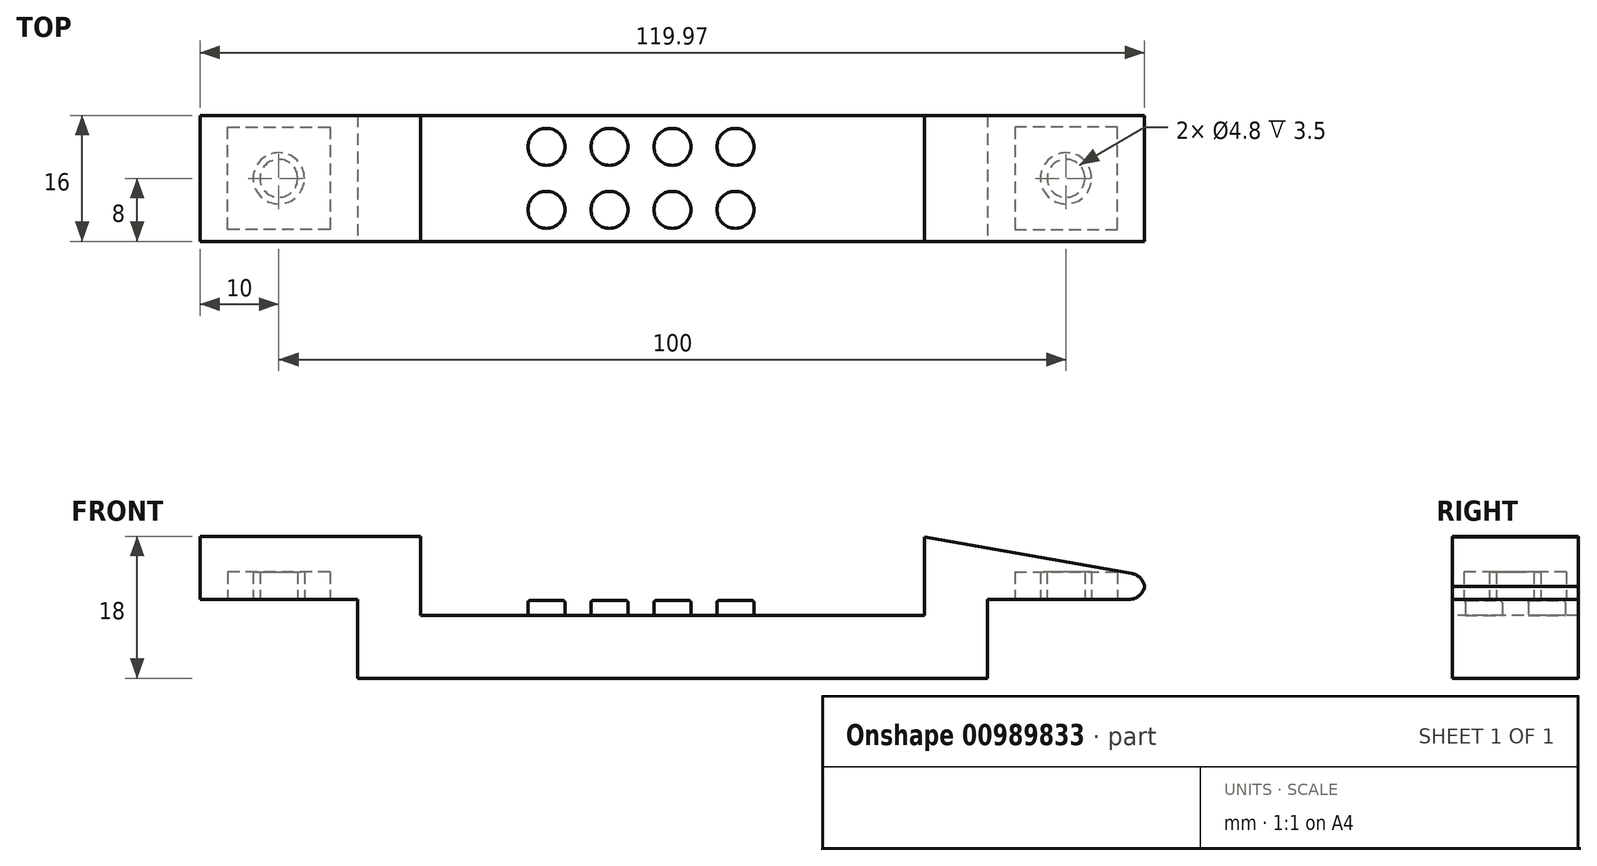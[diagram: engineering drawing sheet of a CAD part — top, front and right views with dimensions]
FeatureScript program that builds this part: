
annotation { "Feature Type Name" : "Feature", "Feature Type Description" : "" }
export const myFeature = defineFeature(function(context is Context, id is Id, definition is map)
    precondition{}
    {
        {
            var Q0;
            Q0=qCreatedBy(makeId("Front.planeOp"),FACE);
            var sketch = newSketch(context, id + "F0", { "sketchPlane" : qUnion([Q0])});
            skLineSegment(sketch, "E0", {"start": v(0, 0) * mm, "end": v(-40, 0) * mm});
            skLineSegment(sketch, "E1", {"start": v(-40, 0) * mm, "end": v(-40, 10) * mm});
            skLineSegment(sketch, "E2", {"start": v(-40, 10) * mm, "end": v(-60, 10) * mm});
            skLineSegment(sketch, "E3.0", {"start": v(-32, 18) * mm, "end": v(-60, 18) * mm});
            skLineSegment(sketch, "E3.1", {"start": v(-32, 8) * mm, "end": v(-32, 18) * mm});
            skLineSegment(sketch, "E3.2", {"start": v(0, 8) * mm, "end": v(-32, 8) * mm});
            skLineSegment(sketch, "E4", {"start": v(-60, 18) * mm, "end": v(-60, 10) * mm});
            skLineSegment(sketch, "E5", {"start": v(0, 8) * mm, "end": v(0, 0) * mm});
            skCircle(sketch, "E6", {"center": v(-50, 6) * mm, "radius": 10 * mm, "construction": true});
            skPoint(sketch, "E6.centerSnap0", {"position": v(-50, 10) * mm});
            skCircle(sketch, "E7", {"center": v(-50, 6) * mm, "radius": 12 * mm, "construction": true});
            skSolve(sketch);
        }
        {
            var Q0;
            Q0=makeQuery(id+"F0.imprint","IMPRINT",FACE,{"disambiguationData":[TD([[makeQuery(id+"F0.imprint","IMPRINT",EDGE,{"derivedFrom":sQuery(id+"F0.wireOp",EDGE,"E0")}),-1.0]])]});
            extrude(context, id + "F1", {"entities" : qUnion([Q0]), "oppositeDirection" : true, "depth" : 16 * mm, "offsetDistance" : 25 * mm});
        }
        {
            var Q0;
            Q0=makeQuery(id+"F1.opExtrude","SWEPT_FACE",FACE,{"disambiguationData":[OSD([sQuery(id+"F0.wireOp",EDGE,"E2")])]});
            var sketch = newSketch(context, id + "F2", { "sketchPlane" : qUnion([Q0])});
            skLineSegment(sketch, "E8", {"start": v(-43.5, -1.5) * mm, "end": v(-56.5, -1.5) * mm});
            skLineSegment(sketch, "E9", {"start": v(-56.5, -1.5) * mm, "end": v(-56.5, -14.5) * mm});
            skLineSegment(sketch, "E10", {"start": v(-56.5, -14.5) * mm, "end": v(-43.5, -14.5) * mm});
            skLineSegment(sketch, "E11", {"start": v(-43.5, -14.5) * mm, "end": v(-43.5, -1.5) * mm});
            skCircle(sketch, "E12.0", {"center": v(-50, -8) * mm, "radius": 2.4 * mm});
            skCircle(sketch, "E13.0", {"center": v(-50, -8) * mm, "radius": 3.25 * mm});
            skLineSegment(sketch, "E14.0", {"start": v(-42, 0) * mm, "end": v(-42, -16) * mm, "construction": true});
            skLineSegment(sketch, "E14.1", {"start": v(-42, 0) * mm, "end": v(-58, 0) * mm, "construction": true});
            skLineSegment(sketch, "E14.2", {"start": v(-58, 0) * mm, "end": v(-58, -16) * mm, "construction": true});
            skLineSegment(sketch, "E14.3", {"start": v(-42, -16) * mm, "end": v(-58, -16) * mm, "construction": true});
            skSolve(sketch);
        }
        {
            var Q0;
            Q0=makeQuery(id+"F2.imprint","IMPRINT",FACE,{"disambiguationData":[TD([[makeQuery(id+"F2.imprint","IMPRINT",EDGE,{"derivedFrom":sQuery(id+"F2.wireOp",EDGE,"E8")}),1.0]])]});
            var Q1;
            Q1=makeQuery(id+"F2.imprint","IMPRINT",FACE,{"disambiguationData":[TD([[makeQuery(id+"F2.imprint","IMPRINT",EDGE,{"derivedFrom":sQuery(id+"F2.wireOp",EDGE,"50b0818d-48c9-435e-a0db-fd159936b803.0")}),1.0]])]});
            var Q2;
            Q2=makeQuery(id+"F2.imprint","IMPRINT",FACE,{"disambiguationData":[TD([[makeQuery(id+"F2.imprint","IMPRINT",EDGE,{"derivedFrom":sQuery(id+"F2.wireOp",EDGE,"E12.0")}),1.0]])]});
            var Q3;
            Q3=makeQuery(id+"F2.imprint","IMPRINT",FACE,{"disambiguationData":[TD([[makeQuery(id+"F2.imprint","IMPRINT",EDGE,{"derivedFrom":sQuery(id+"F2.wireOp",EDGE,"9362b03a-9ce0-4955-ab87-d27d4ad72b78.0")}),1.0]])]});
            extrude(context, id + "F3", {"entities" : qUnion([Q0, Q1, Q2, Q3]), "operationType" : NewBodyOperationType.REMOVE, "oppositeDirection" : true, "depth" : 3.5 * mm, "offsetDistance" : 25 * mm});
        }
        {
            var Q0;
            Q0=makeQuery(id+"F1.opExtrude","SWEPT_BODY",BODY,{"disambiguationData":[OSD([sQuery(id+"F0.wireOp",EDGE,"E0"),sQuery(id+"F0.wireOp",EDGE,"E1"),sQuery(id+"F0.wireOp",EDGE,"E2"),sQuery(id+"F0.wireOp",EDGE,"E3.0"),sQuery(id+"F0.wireOp",EDGE,"E3.1"),sQuery(id+"F0.wireOp",EDGE,"E3.2"),sQuery(id+"F0.wireOp",EDGE,"E4"),sQuery(id+"F0.wireOp",EDGE,"E5")])]});
            var Q1;
            Q1=makeQuery(id+"F1.opExtrude","SWEPT_FACE",FACE,{"disambiguationData":[OSD([sQuery(id+"F0.wireOp",EDGE,"E5")])]});
            mirror(context, id + "F4", {"operationType" : NewBodyOperationType.ADD, "entities" : qUnion([Q0]), "mirrorPlane" : qUnion([Q1])});
        }
        {
            var Q0;
            {var subQ0=makeQuery(id+"F1.opExtrude","SWEPT_FACE",FACE,{"disambiguationData":[OSD([sQuery(id+"F0.wireOp",EDGE,"E3.2")])]});Q0=makeQuery(id+"F4.boolean.opBoolean","MERGE",FACE,{"derivedFrom":[subQ0,makeQuery(id+"F4.opPattern","COPY",FACE,{"derivedFrom":subQ0,"instanceName":"1"})]});}
            var sketch = newSketch(context, id + "F5", { "sketchPlane" : qUnion([Q0])});
            skLineSegment(sketch, "E15.0", {"start": v(-19.9, 0) * mm, "end": v(12.1, 0) * mm, "construction": true});
            skLineSegment(sketch, "E15.1", {"start": v(-19.9, 0) * mm, "end": v(-19.9, 16) * mm, "construction": true});
            skLineSegment(sketch, "E15.2", {"start": v(-19.9, 16) * mm, "end": v(12.1, 16) * mm, "construction": true});
            skLineSegment(sketch, "E15.3", {"start": v(12.1, 0) * mm, "end": v(12.1, 16) * mm, "construction": true});
            skCircle(sketch, "E15.4", {"center": v(8, 4) * mm, "radius": 2.35 * mm});
            skCircle(sketch, "E15.5", {"center": v(8, 12) * mm, "radius": 2.35 * mm});
            skCircle(sketch, "E15.6", {"center": v(0, 12) * mm, "radius": 2.35 * mm});
            skCircle(sketch, "E15.7", {"center": v(0, 4) * mm, "radius": 2.35 * mm});
            skCircle(sketch, "E15.8", {"center": v(-8, 4) * mm, "radius": 2.35 * mm});
            skCircle(sketch, "E15.9", {"center": v(-8, 12) * mm, "radius": 2.35 * mm});
            skCircle(sketch, "E15.10", {"center": v(-16, 12) * mm, "radius": 2.35 * mm});
            skCircle(sketch, "E15.11", {"center": v(-16, 4) * mm, "radius": 2.35 * mm});
            skSolve(sketch);
        }
        {
            var Q0;
            Q0=makeQuery(id+"F5.imprint","IMPRINT",FACE,{"disambiguationData":[TD([[makeQuery(id+"F5.imprint","IMPRINT",EDGE,{"derivedFrom":sQuery(id+"F5.wireOp",EDGE,"E15.11")}),1.0]])]});
            var Q1;
            Q1=makeQuery(id+"F5.imprint","IMPRINT",FACE,{"disambiguationData":[TD([[makeQuery(id+"F5.imprint","IMPRINT",EDGE,{"derivedFrom":sQuery(id+"F5.wireOp",EDGE,"E15.10")}),1.0]])]});
            var Q2;
            Q2=makeQuery(id+"F5.imprint","IMPRINT",FACE,{"disambiguationData":[TD([[makeQuery(id+"F5.imprint","IMPRINT",EDGE,{"derivedFrom":sQuery(id+"F5.wireOp",EDGE,"E15.9")}),1.0]])]});
            var Q3;
            Q3=makeQuery(id+"F5.imprint","IMPRINT",FACE,{"disambiguationData":[TD([[makeQuery(id+"F5.imprint","IMPRINT",EDGE,{"derivedFrom":sQuery(id+"F5.wireOp",EDGE,"E15.8")}),1.0]])]});
            var Q4;
            Q4=makeQuery(id+"F5.imprint","IMPRINT",FACE,{"disambiguationData":[TD([[makeQuery(id+"F5.imprint","IMPRINT",EDGE,{"derivedFrom":sQuery(id+"F5.wireOp",EDGE,"E15.7")}),1.0]])]});
            var Q5;
            Q5=makeQuery(id+"F5.imprint","IMPRINT",FACE,{"disambiguationData":[TD([[makeQuery(id+"F5.imprint","IMPRINT",EDGE,{"derivedFrom":sQuery(id+"F5.wireOp",EDGE,"E15.6")}),1.0]])]});
            var Q6;
            Q6=makeQuery(id+"F5.imprint","IMPRINT",FACE,{"disambiguationData":[TD([[makeQuery(id+"F5.imprint","IMPRINT",EDGE,{"derivedFrom":sQuery(id+"F5.wireOp",EDGE,"E15.5")}),1.0]])]});
            var Q7;
            Q7=makeQuery(id+"F5.imprint","IMPRINT",FACE,{"disambiguationData":[TD([[makeQuery(id+"F5.imprint","IMPRINT",EDGE,{"derivedFrom":sQuery(id+"F5.wireOp",EDGE,"E15.4")}),1.0]])]});
            extrude(context, id + "F6", {"entities" : qUnion([Q0, Q1, Q2, Q3, Q4, Q5, Q6, Q7]), "operationType" : NewBodyOperationType.ADD, "depth" : 1.85 * mm, "offsetDistance" : 25 * mm});
        }
        {
            var Q0;
            Q0=makeQuery(id+"F4.opPattern","COPY",EDGE,{"derivedFrom":makeQuery(id+"F1.opExtrude","SWEPT_EDGE",EDGE,{"disambiguationData":[OSD([sQuery(id+"F0.wireOp",EDGE,"E3.0"),sQuery(id+"F0.wireOp",EDGE,"E4")])]}),"instanceName":"1"});
            chamfer(context, id + "F7", {"entities" : qUnion([Q0]), "chamferType" : ChamferType.OFFSET_ANGLE, "width" : 5 * mm, "oppositeDirection" : false, "angle" : 80 * degree, "tangentPropagation" : true});
        }
        {
            var Q0;
            {var subQ0=sQuery(id+"F0.wireOp",EDGE,"E3.0");Q0=makeQuery(id+"F7.opChamfer","BLEND_EDGE",EDGE,{"blendedFrom":[makeQuery(id+"F4.opPattern","COPY",EDGE,{"derivedFrom":makeQuery(id+"F1.opExtrude","SWEPT_EDGE",EDGE,{"disambiguationData":[OSD([subQ0,sQuery(id+"F0.wireOp",EDGE,"E4")])]}),"instanceName":"1"}),makeQuery(id+"F4.opPattern","COPY",FACE,{"derivedFrom":makeQuery(id+"F1.opExtrude","SWEPT_FACE",FACE,{"disambiguationData":[OSD([subQ0])]}),"instanceName":"1"})],"blendedInto":[makeQuery(id+"F4.opPattern","COPY",FACE,{"derivedFrom":makeQuery(id+"F1.opExtrude","SWEPT_FACE",FACE,{"disambiguationData":[OSD([subQ0])]}),"instanceName":"1"})]});}
            var Q1;
            {var subQ0=sQuery(id+"F0.wireOp",EDGE,"E4");Q1=makeQuery(id+"F7.opChamfer","BLEND_EDGE",EDGE,{"blendedFrom":[makeQuery(id+"F4.opPattern","COPY",EDGE,{"derivedFrom":makeQuery(id+"F1.opExtrude","SWEPT_EDGE",EDGE,{"disambiguationData":[OSD([sQuery(id+"F0.wireOp",EDGE,"E3.0"),subQ0])]}),"instanceName":"1"}),makeQuery(id+"F4.opPattern","COPY",FACE,{"derivedFrom":makeQuery(id+"F1.opExtrude","SWEPT_FACE",FACE,{"disambiguationData":[OSD([subQ0])]}),"instanceName":"1"})],"blendedInto":[makeQuery(id+"F4.opPattern","COPY",FACE,{"derivedFrom":makeQuery(id+"F1.opExtrude","SWEPT_FACE",FACE,{"disambiguationData":[OSD([subQ0])]}),"instanceName":"1"})]});}
            var Q2;
            Q2=makeQuery(id+"F4.opPattern","COPY",EDGE,{"derivedFrom":makeQuery(id+"F1.opExtrude","SWEPT_EDGE",EDGE,{"disambiguationData":[OSD([sQuery(id+"F0.wireOp",EDGE,"E2"),sQuery(id+"F0.wireOp",EDGE,"E4")])]}),"instanceName":"1"});
            fillet(context, id + "F8", {"entities" : qUnion([Q0, Q1, Q2]), "radius" : 2 * mm, "tangentPropagation" : true, "allowEdgeOverflow" : false});
        }
        {
            var Q0;
            Q0=makeQuery(id+"F6.opExtrude","CAP_EDGE",EDGE,{"disambiguationData":[OSD([sQuery(id+"F5.wireOp",EDGE,"E15.11")])],"isStart":false});
            var Q1;
            Q1=makeQuery(id+"F6.opExtrude","CAP_EDGE",EDGE,{"disambiguationData":[OSD([sQuery(id+"F5.wireOp",EDGE,"E15.10")])],"isStart":false});
            var Q2;
            Q2=makeQuery(id+"F6.opExtrude","CAP_EDGE",EDGE,{"disambiguationData":[OSD([sQuery(id+"F5.wireOp",EDGE,"E15.9")])],"isStart":false});
            var Q3;
            Q3=makeQuery(id+"F6.opExtrude","CAP_EDGE",EDGE,{"disambiguationData":[OSD([sQuery(id+"F5.wireOp",EDGE,"E15.8")])],"isStart":false});
            var Q4;
            Q4=makeQuery(id+"F6.opExtrude","CAP_EDGE",EDGE,{"disambiguationData":[OSD([sQuery(id+"F5.wireOp",EDGE,"E15.7")])],"isStart":false});
            var Q5;
            Q5=makeQuery(id+"F6.opExtrude","CAP_EDGE",EDGE,{"disambiguationData":[OSD([sQuery(id+"F5.wireOp",EDGE,"E15.6")])],"isStart":false});
            var Q6;
            Q6=makeQuery(id+"F6.opExtrude","CAP_EDGE",EDGE,{"disambiguationData":[OSD([sQuery(id+"F5.wireOp",EDGE,"E15.5")])],"isStart":false});
            var Q7;
            Q7=makeQuery(id+"F6.opExtrude","CAP_EDGE",EDGE,{"disambiguationData":[OSD([sQuery(id+"F5.wireOp",EDGE,"E15.4")])],"isStart":false});
            fillet(context, id + "F9", {"entities" : qUnion([Q0, Q1, Q2, Q3, Q4, Q5, Q6, Q7]), "radius" : .25 * mm, "tangentPropagation" : true, "allowEdgeOverflow" : false});
        }
    });
